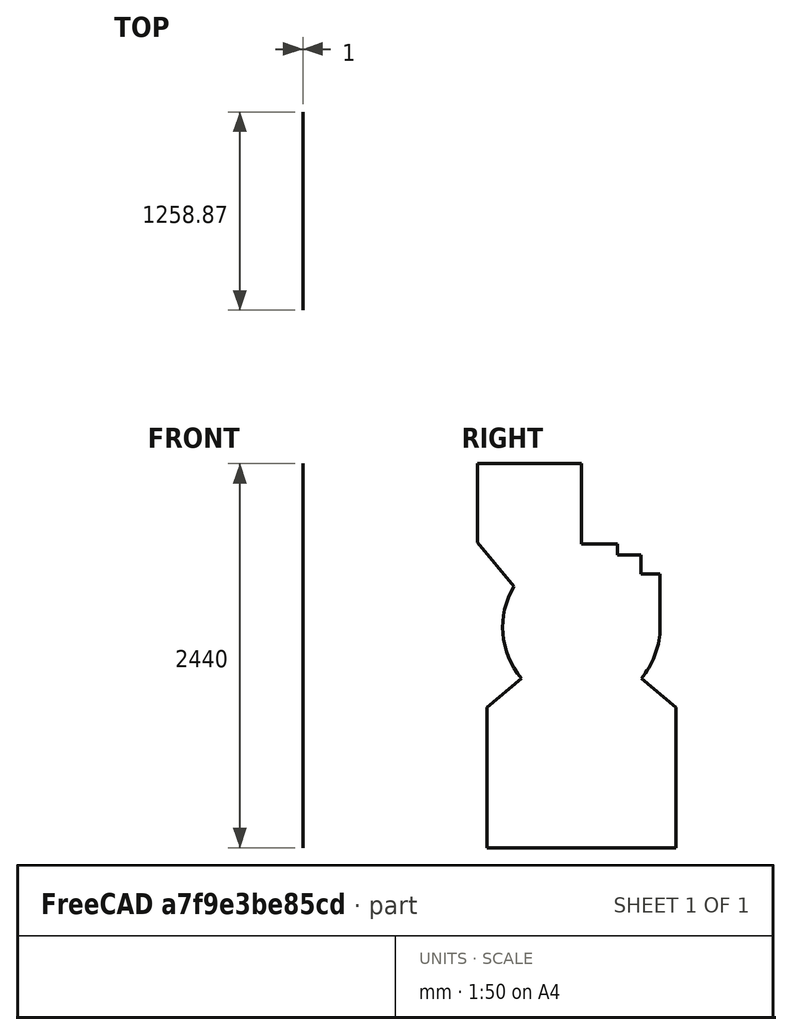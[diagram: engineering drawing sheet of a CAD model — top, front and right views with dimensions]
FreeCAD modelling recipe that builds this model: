
FCSTD DOCUMENT
Label: Shell_back
objects: Sketcher::SketchObject×1, PartDesign::Pad×1
note: 3 computed .brp shape members not serialized (recipe doc carries the construction recipe); baked Part::Feature solids carry a one-line shape summary decoded from their .brp

FEATURE [Sketcher::SketchObject] Sketch  label="Shell_back"
  Placement = pos=(-500,0,0) rot=(0.57735,0.57735,0.57735;2.0944rad)
  sketch-geometry (17):
    g0: ArcOfCircle CenterX=0 CenterY=0 CenterZ=0 NormalX=0 NormalY=0 NormalZ=1 Radius=500 StartAngle=2.59474 EndAngle=3.84621
    g1: LineSegment StartX=-427.083 StartY=260 StartZ=0 EndX=-658.874 EndY=540 EndZ=0
    g2: LineSegment StartX=0 StartY=530 StartZ=0 EndX=230 EndY=530 EndZ=0
    g3: LineSegment StartX=230 StartY=530 StartZ=0 EndX=230 EndY=460 EndZ=0
    g4: LineSegment StartX=230 StartY=460 StartZ=0 EndX=380 EndY=460 EndZ=0
    g5: LineSegment StartX=380 StartY=460 StartZ=0 EndX=380 EndY=340 EndZ=0
    g6: LineSegment StartX=380 StartY=340 StartZ=0 EndX=499.438 EndY=340 EndZ=0
    g7: LineSegment StartX=499.438 StartY=340 StartZ=0 EndX=499.438 EndY=-23.6939 EndZ=0
    g8: LineSegment StartX=-658.874 StartY=1040 StartZ=0 EndX=-658.874 EndY=540 EndZ=0
    g9: LineSegment StartX=-380.931 StartY=-323.87 StartZ=0 EndX=-600 EndY=-507.691 EndZ=0
    g10: LineSegment StartX=-600 StartY=-507.691 StartZ=0 EndX=-600 EndY=-1400 EndZ=0
    g11: LineSegment StartX=-600 StartY=-1400 StartZ=0 EndX=600 EndY=-1400 EndZ=0
    g12: LineSegment StartX=600 StartY=-1400 StartZ=0 EndX=600 EndY=-507.691 EndZ=0
    g13: LineSegment StartX=600 StartY=-507.691 StartZ=0 EndX=380.931 EndY=-323.87 EndZ=0
    g14: ArcOfCircle CenterX=0 CenterY=0 CenterZ=0 NormalX=0 NormalY=0 NormalZ=1 Radius=500 StartAngle=5.57857 EndAngle=6.23578
    g15: LineSegment StartX=-658.874 StartY=1040 StartZ=0 EndX=0 EndY=1040 EndZ=0
    g16: LineSegment StartX=0 StartY=1040 StartZ=0 EndX=0 EndY=530 EndZ=0
  constraints (52):
    c: Radius(g0) = 500
    c: DistanceX(g0) = 0
    c: DistanceY(g0) = 0
    c: Horizontal(g2)
    c: Vertical(g3)
    c: Coincident(g4,g3)
    c: Horizontal(g4)
    c: Vertical(g5)
    c: Coincident(g6,g5)
    c: Horizontal(g6)
    c: DistanceY(g1) = 540
    c: Coincident(g2,g3)
    c: Coincident(g4,g5)
    c: Vertical(g7)
    c: Coincident(g1,g0)
    c: Coincident(g8,g1)
    c: Vertical(g8)
    c: Distance(g1) = 363.493
    c: Distance(g8) = 500
    c: Coincident(g10,g9)
    c: Vertical(g10)
    c: Horizontal(g11)
    c: Coincident(g12,g11)
    c: Vertical(g12)
    c: Coincident(g13,g12)
    c: Coincident(g11,g10)
    c: Equal(g12,g10)
    c: DistanceX(g11) = 600
    c: DistanceY(g11) = -1400
    c: Angle(g10,g9) = 2.26893
    c: Angle(g13,g12) = 2.26893
    c: Distance(g10) = 892.309
    c: Distance(g11) = 1200
    c: Equal(g0,g14)
    c: Coincident(g0,g14)
    c: Coincident(g15,g8)
    c: Horizontal(g15)
    c: Coincident(g16,g15)
    c: Vertical(g16)
    c: Coincident(g6,g7)
    c: Coincident(g16,g2)
    c: DistanceX(g5) = 380
    c: DistanceY(g5) = 340
    c: DistanceX(g3) = 230
    c: DistanceY(g3) = 460
    c: DistanceX(g2) = 0
    c: DistanceY(g2) = 530
    c: DistanceY(g0) = 260
    c: Coincident(g9,g0)
    c: Coincident(g14,g13)
    c: Coincident(g14,g7)
    c: Distance(g7) = 363.694
FEATURE [PartDesign::Pad] Pad  label="Shell_back_"
  Length = 1
  MirroredExtent = false
  Reversed = true
  Sketch = -> Sketch
